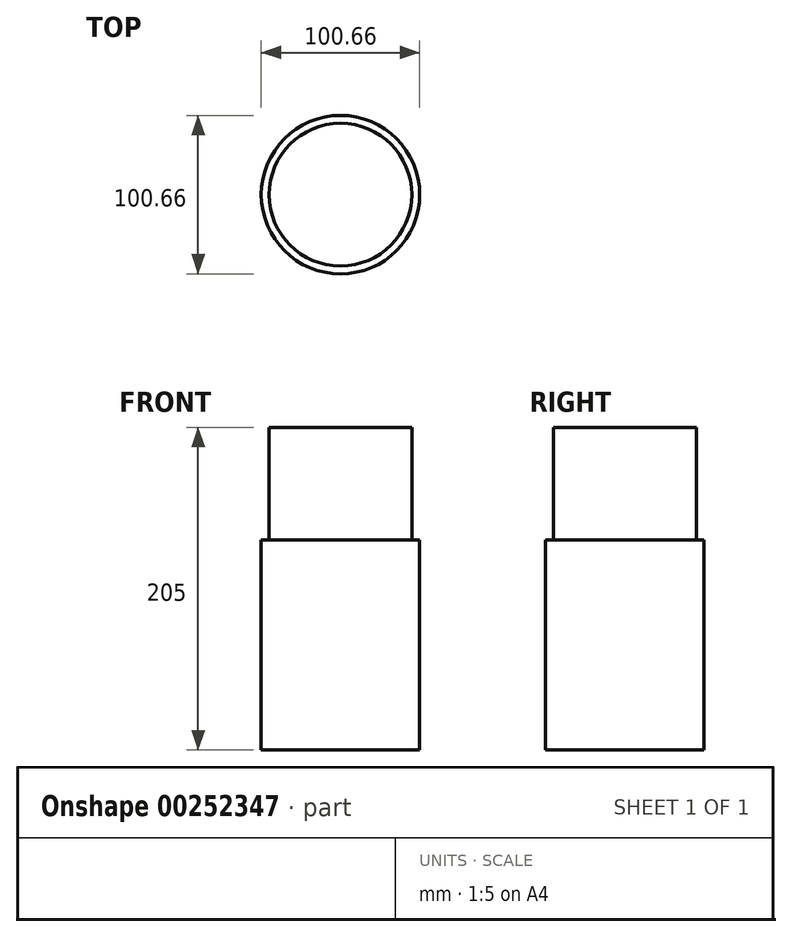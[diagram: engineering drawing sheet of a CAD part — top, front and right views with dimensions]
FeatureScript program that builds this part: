
annotation { "Feature Type Name" : "Feature", "Feature Type Description" : "" }
export const myFeature = defineFeature(function(context is Context, id is Id, definition is map)
    precondition{}
    {
        {
            var Q0;
            Q0=qCreatedBy(makeId("Front.planeOp"),FACE);
            var sketch = newSketch(context, id + "F0", { "sketchPlane" : qUnion([Q0])});
            skLineSegment(sketch, "E0.bottom", {"start": v(-45.33, 56.09) * mm, "end": v(46.48, 56.09) * mm});
            skLineSegment(sketch, "E0.top", {"start": v(-45.33, -72.44) * mm, "end": v(46.48, -72.44) * mm});
            skLineSegment(sketch, "E0.left", {"start": v(-45.33, 56.09) * mm, "end": v(-45.33, -72.44) * mm});
            skLineSegment(sketch, "E0.right", {"start": v(46.48, 56.09) * mm, "end": v(46.48, -72.44) * mm});
            skLineSegment(sketch, "E1", {"start": v(0, 56.09) * mm, "end": v(0, -72.44) * mm});
            skPoint(sketch, "E1.startSnap0", {"position": v(0.57, 56.09) * mm});
            skSolve(sketch);
        }
        {
            var Q0;
            {var subQ0=sQuery(id+"F0.wireOp",EDGE,"E0.left");Q0=makeQuery(id+"F0.imprint","IMPRINT",FACE,{"disambiguationData":[TD([[makeQuery(id+"F0.imprint","IMPRINT",EDGE,{"derivedFrom":subQ0}),1.0]])]});}
            var Q1;
            Q1=sQuery(id+"F0.wireOp",EDGE,"E1");
            revolve(context, id + "F1", {"entities" : qUnion([Q0]), "axis" : qUnion([Q1]), "revolveType" : RevolveType.FULL});
        }
        {
            var Q0;
            Q0=makeQuery(id+"F1.opRevolve","SWEPT_FACE",FACE,{"disambiguationData":[OSD([sQuery(id+"F0.wireOp",EDGE,"E0.bottom")])]});
            shell(context, id + "F2", {"entities" : qUnion([Q0]), "thickness" : 5 * mm, "oppositeDirection" : true});
        }
        {
            var Q0;
            Q0=makeQuery(id+"F2.opShell","OFFSET_FACE",FACE,{"disambiguationData":[OSD([sQuery(id+"F0.wireOp",EDGE,"E0.top")])]});
            extrude(context, id + "F3", {"entities" : qUnion([Q0]), "operationType" : NewBodyOperationType.ADD, "depth" : 200 * mm});
        }
    });
